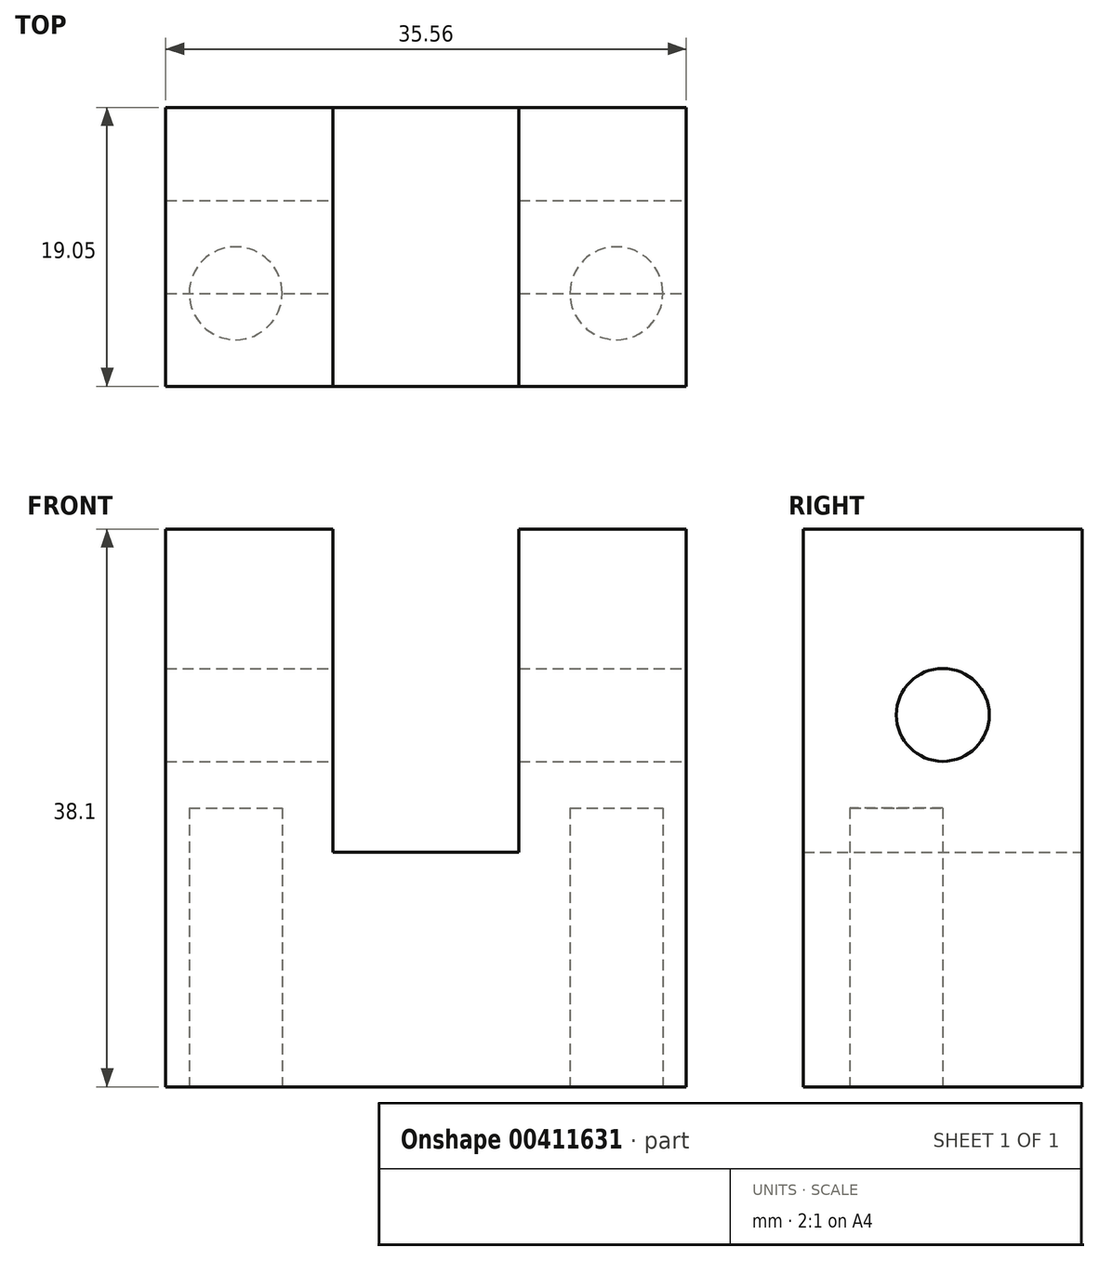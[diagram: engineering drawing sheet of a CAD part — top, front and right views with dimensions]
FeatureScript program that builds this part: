
annotation { "Feature Type Name" : "Feature", "Feature Type Description" : "" }
export const myFeature = defineFeature(function(context is Context, id is Id, definition is map)
    precondition{}
    {
        {
            var Q0;
            Q0=qCreatedBy(makeId("Front.planeOp"),FACE);
            var sketch = newSketch(context, id + "F0", { "sketchPlane" : qUnion([Q0])});
            skLineSegment(sketch, "E0", {"start": v(-41.75, 20.45) * mm, "end": v(-30.32, 20.45) * mm});
            skLineSegment(sketch, "E1", {"start": v(-30.32, 20.45) * mm, "end": v(-30.32, -1.62) * mm});
            skLineSegment(sketch, "E2", {"start": v(-30.32, -1.62) * mm, "end": v(-17.62, -1.62) * mm});
            skLineSegment(sketch, "E3", {"start": v(-17.62, -1.62) * mm, "end": v(-17.62, 20.45) * mm});
            skLineSegment(sketch, "E4", {"start": v(-17.62, 20.45) * mm, "end": v(-6.19, 20.45) * mm});
            skLineSegment(sketch, "E5", {"start": v(-6.19, 20.45) * mm, "end": v(-6.19, -17.65) * mm});
            skLineSegment(sketch, "E6", {"start": v(-6.19, -17.65) * mm, "end": v(-41.75, -17.65) * mm});
            skLineSegment(sketch, "E7", {"start": v(-41.75, -17.65) * mm, "end": v(-41.75, 20.45) * mm});
            skSolve(sketch);
        }
        {
            var Q0;
            Q0 = qSketchRegion(id + "F0", true);
            extrude(context, id + "F1", {"entities" : qUnion([Q0]), "depth" : 19.05 * mm});
        }
        {
            var Q0;
            Q0=makeQuery(id+"F1.opExtrude","SWEPT_FACE",FACE,{"disambiguationData":[OSD([sQuery(id+"F0.wireOp",EDGE,"E5")])]});
            var sketch = newSketch(context, id + "F2", { "sketchPlane" : qUnion([Q0])});
            skCircle(sketch, "E8", {"center": v(-9.53, 7.75) * mm, "radius": 3.18 * mm});
            skSolve(sketch);
        }
        {
            var Q0;
            Q0=makeQuery(id+"F2.imprint","IMPRINT",FACE,{"disambiguationData":[TD([[makeQuery(id+"F2.imprint","IMPRINT",EDGE,{"derivedFrom":sQuery(id+"F2.wireOp",EDGE,"E8")}),1.0]])]});
            extrude(context, id + "F3", {"entities" : qUnion([Q0]), "operationType" : NewBodyOperationType.REMOVE, "endBound" : BoundingType.THROUGH_ALL, "oppositeDirection" : true, "depth" : 25.4 * mm});
        }
        {
            var Q0;
            Q0=makeQuery(id+"F1.opExtrude","SWEPT_FACE",FACE,{"disambiguationData":[OSD([sQuery(id+"F0.wireOp",EDGE,"E6")])]});
            var sketch = newSketch(context, id + "F4", { "sketchPlane" : qUnion([Q0])});
            skCircle(sketch, "E9", {"center": v(-36.97, 12.7) * mm, "radius": 3.18 * mm});
            skCircle(sketch, "E10", {"center": v(-10.96, 12.7) * mm, "radius": 3.18 * mm});
            skSolve(sketch);
        }
        {
            var Q0;
            Q0 = qSketchRegion(id + "F4", true);
            extrude(context, id + "F5", {"entities" : qUnion([Q0]), "operationType" : NewBodyOperationType.REMOVE, "oppositeDirection" : true, "depth" : 19.05 * mm});
        }
    });
